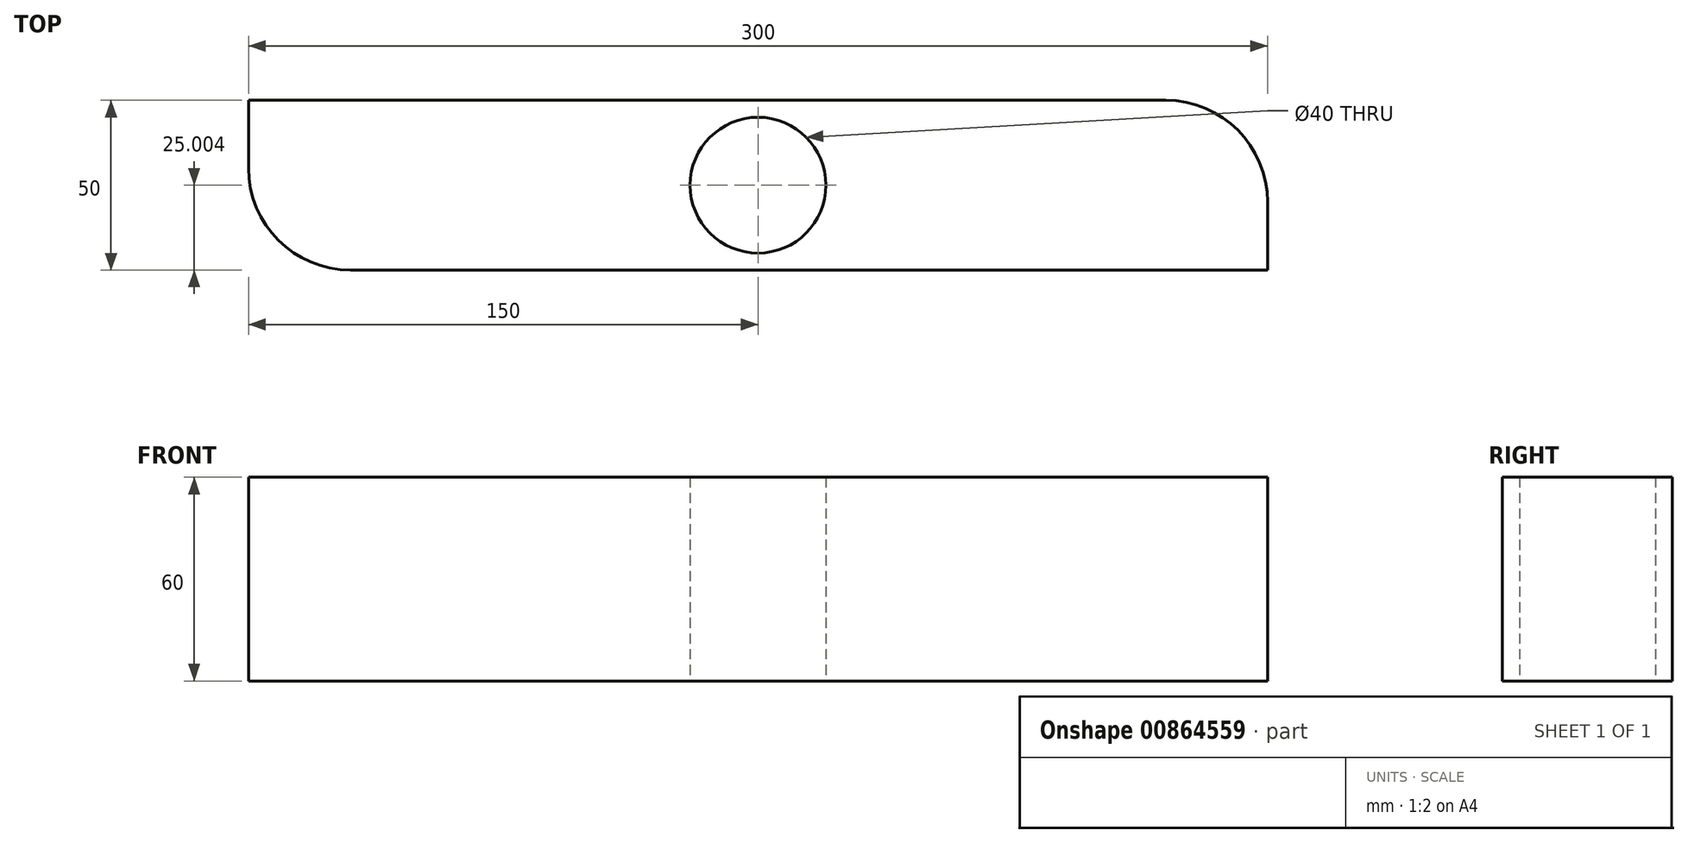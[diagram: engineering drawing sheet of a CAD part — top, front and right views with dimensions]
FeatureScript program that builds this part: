
annotation { "Feature Type Name" : "Feature", "Feature Type Description" : "" }
export const myFeature = defineFeature(function(context is Context, id is Id, definition is map)
    precondition{}
    {
        {
            var Q0;
            Q0=qCreatedBy(makeId("Top.planeOp"),FACE);
            var sketch = newSketch(context, id + "F0", { "sketchPlane" : qUnion([Q0])});
            skLineSegment(sketch, "E0.bottom", {"start": v(-150, 0.9) * mm, "end": v(150, 0.9) * mm});
            skLineSegment(sketch, "E0.top", {"start": v(-150, -49.1) * mm, "end": v(150, -49.1) * mm});
            skLineSegment(sketch, "E0.left", {"start": v(-150, 0.9) * mm, "end": v(-150, -49.1) * mm});
            skLineSegment(sketch, "E0.right", {"start": v(150, 0.9) * mm, "end": v(150, -49.1) * mm});
            skCircle(sketch, "E1", {"center": v(0, -24.1) * mm, "radius": 20 * mm});
            skLineSegment(sketch, "E2", {"start": v(-150, 0.9) * mm, "end": v(150, -49.1) * mm, "construction": true});
            skSolve(sketch);
        }
        {
            var Q0;
            Q0=makeQuery(id+"F0.imprint","IMPRINT",FACE,{"disambiguationData":[TD([[makeQuery(id+"F0.imprint","IMPRINT",EDGE,{"derivedFrom":sQuery(id+"F0.wireOp",EDGE,"E0.bottom")}),-1.0]])]});
            extrude(context, id + "F1", {"entities" : qUnion([Q0]), "depth" : 60 * mm, "offsetDistance" : 25.4 * mm});
        }
        {
            var Q0;
            Q0=makeQuery(id+"F1.opExtrude","SWEPT_EDGE",EDGE,{"disambiguationData":[OSD([sQuery(id+"F0.wireOp",EDGE,"E0.top"),sQuery(id+"F0.wireOp",EDGE,"E0.left")])]});
            var Q1;
            Q1=makeQuery(id+"F1.opExtrude","SWEPT_EDGE",EDGE,{"disambiguationData":[OSD([sQuery(id+"F0.wireOp",EDGE,"E0.bottom"),sQuery(id+"F0.wireOp",EDGE,"E0.right")])]});
            fillet(context, id + "F2", {"entities" : qUnion([Q0, Q1]), "radius" : 30 * mm, "tangentPropagation" : true, "allowEdgeOverflow" : false});
        }
    });
